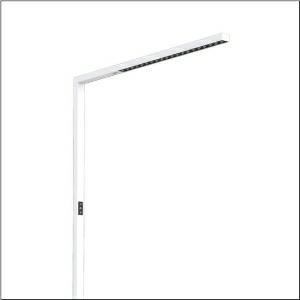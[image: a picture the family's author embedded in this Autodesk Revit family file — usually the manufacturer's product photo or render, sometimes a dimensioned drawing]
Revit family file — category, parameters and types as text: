
# Revit family: silica_r__31_floor_51my52fa3cw_3d14
name_source: partatom
category: Lighting Fixtures
units: mm (PartAtom-declared; Revit-internal decimal feet)

## family parameters
Cut with Voids When Loaded = No
Host = Face
Light Source = No
Part Type = Normal
Room Calculation Point = No
Round Connector Dimension = Use Diameter
Shared = No

## types (1)
- Silica® 31 Floor (1 x LED, 10300 lm, 75 W, 3000K)
    Apparent Load = 75 VA
    CIE Flux Codes = 86 100 100 24 100
    Color Rendering = 80
    Color Temperature = 3000K
    Default Elevation = 1800 mm
    Description = Silica® 31 Floor, floorstanding luminaire, secondary optical cover: cover panel, of PMMA, light emission: direct/indirect distribution, primary light characteristic: symmetric, installation type: not mounted, LED, rated luminous flux: 10.300lm, luminous efficacy: 137lm/W, light colour: 830, colour temperature: 3000K, control gear: Touchdim, daylight-dependent control, with cable with plug, mains connection: 230V, AC, 50Hz, connection cable pre-assembled, rated input power: 75W, luminaire head, of aluminium, traffic white (RAL 9016), length: 1.203mm, width: 52mm, supporting column, angular, of aluminium, traffic white (RAL 9016), baseplate, of steel, traffic white (RAL 9016), protection rating (complete): IP20, insulation class (complete): insulation class I (protective earthing), certification: CE, permissible operating ambient temperature: -20..+40°C, standard: EN 50419, packaging unit: 1 piece
    Height = 36 mm
    Lamp = 1 x LED
    Lamp Light Flux = 10300 lm
    Lamp Power = 75 W
    Lamp count = 1
    Length = 1203 mm
    Luminous efficacy = 137 lm/W
    Manufacturer = Siteco
    ModVariant = No
    Model = 51MY52FA3CW
    Mounting Place = Floor
    Mounting Type = Freestanding
    Number of Poles = 1
    OnlyDefault = Yes
    Power Factor = 1
    Product Name = Silica® 31 Floor
    Product group = floorstanding luminaire
    ProductGroupID = 1302
    Protection Class = Protection class I
    Protection Degree = IP 20
    RLX_Detail_Level = 1
    RLX_Emergency_Light_Flux = 0 lm
    RLX_Emergency_Type = 0
    RLX_Emergency_Type_DB = No
    RlxData = <blob elided: 17101 chars, md5=cef775fe>
    Socket = socket
    Standby Power = 0 W
    System Light Flux = 10300 lm
    System Power = 75 W
    Type Comments = Product without accessories
    Type Image = l_1275309.jpg
    URL = http://relux.com
    VarID = ---
    Voltage = 0 V
    Weight = 0.00 kg
    Width = 52 mm  [stored 0.170604 ft]

note: [stored X ft] marks values corroborated as IEEE doubles in the binary element streams (Revit-internal decimal feet)

## geometry (parser evidence)
native form markers: Blend x4, Sweep x15
no freeform markers — native parametric forms only
